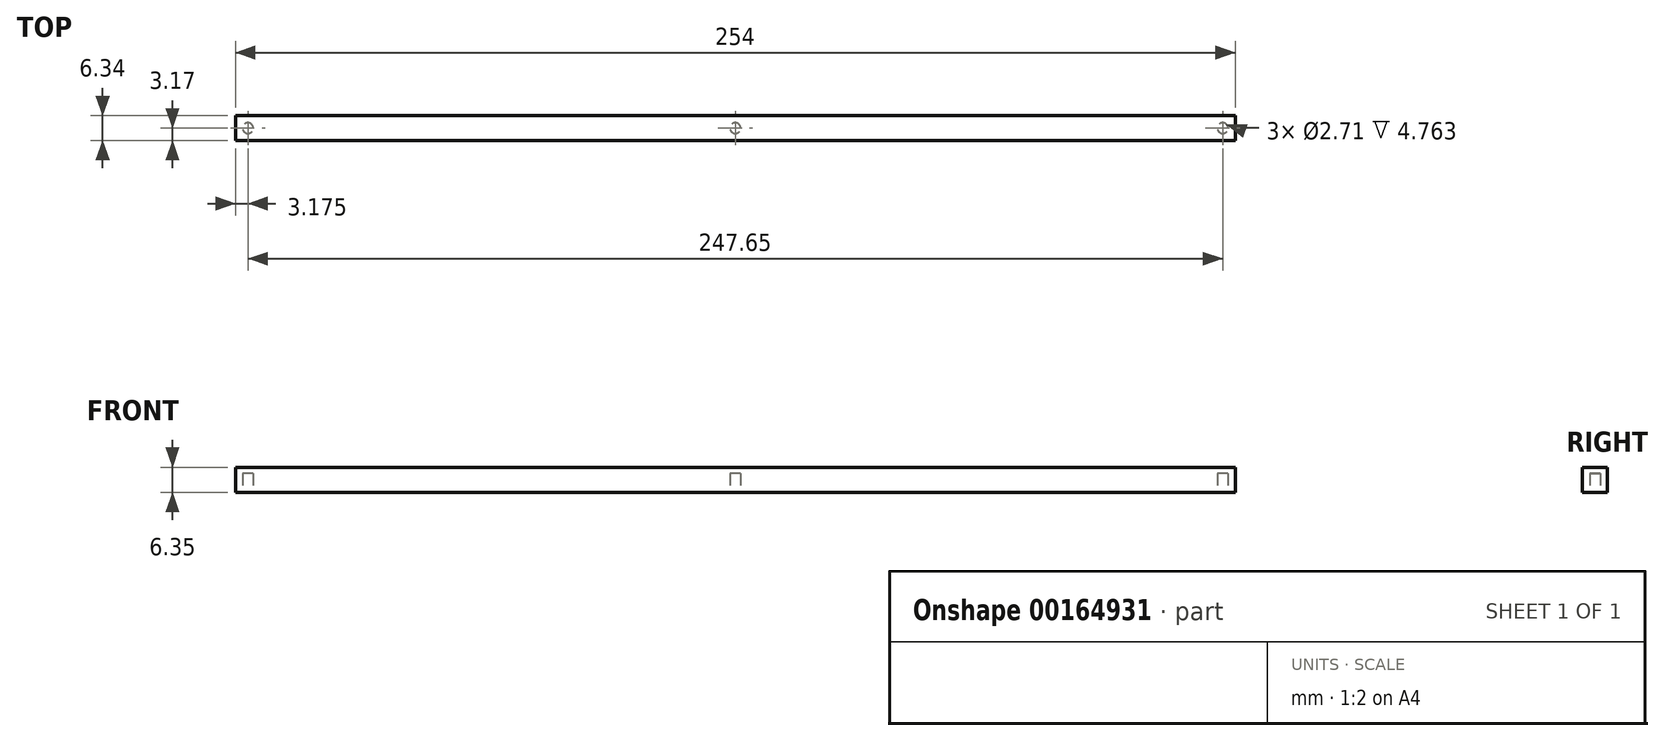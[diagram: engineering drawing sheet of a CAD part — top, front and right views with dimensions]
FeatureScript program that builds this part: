
annotation { "Feature Type Name" : "Feature", "Feature Type Description" : "" }
export const myFeature = defineFeature(function(context is Context, id is Id, definition is map)
    precondition{}
    {
        {
            var Q0;
            Q0=qCreatedBy(makeId("Top.planeOp"),FACE);
            var sketch = newSketch(context, id + "F0", { "sketchPlane" : qUnion([Q0])});
            skLineSegment(sketch, "E0.bottom", {"start": v(127, -3.17) * mm, "end": v(-127, -3.18) * mm});
            skLineSegment(sketch, "E0.top", {"start": v(127, 3.18) * mm, "end": v(-127, 3.17) * mm});
            skLineSegment(sketch, "E0.left", {"start": v(127, -3.17) * mm, "end": v(127, 3.18) * mm});
            skLineSegment(sketch, "E0.right", {"start": v(-127, -3.18) * mm, "end": v(-127, 3.17) * mm});
            skPoint(sketch, "E0.middle", {"position": v(0, 0) * mm});
            skCircle(sketch, "E1", {"center": v(0, 0) * mm, "radius": 1.35 * mm});
            skLineSegment(sketch, "E2", {"start": v(-127, 0) * mm, "end": v(-123.83, 0) * mm, "construction": true});
            skPoint(sketch, "E2.endSnap0", {"position": v(-127, 0) * mm});
            skLineSegment(sketch, "E3", {"start": v(-123.83, 0) * mm, "end": v(-123.83, 3.17) * mm, "construction": true});
            skLineSegment(sketch, "E4", {"start": v(127, 0) * mm, "end": v(123.82, 0) * mm, "construction": true});
            skPoint(sketch, "E4.endSnap0", {"position": v(127, 0) * mm});
            skCircle(sketch, "E5", {"center": v(-123.83, 0) * mm, "radius": 1.35 * mm});
            skCircle(sketch, "E6", {"center": v(123.82, 0) * mm, "radius": 1.35 * mm});
            skSolve(sketch);
        }
        {
            var Q0;
            Q0 = qSketchRegion(id + "F0", true);
            extrude(context, id + "F1", {"entities" : qUnion([Q0]), "depth" : 4.76 * mm});
        }
        {
            var Q0;
            Q0=makeQuery(id+"F1.opExtrude","CAP_FACE",FACE,{"disambiguationData":[OSD([sQuery(id+"F0.wireOp",EDGE,"E0.bottom"),sQuery(id+"F0.wireOp",EDGE,"E0.top"),sQuery(id+"F0.wireOp",EDGE,"E0.left"),sQuery(id+"F0.wireOp",EDGE,"E0.right"),sQuery(id+"F0.wireOp",EDGE,"E1"),sQuery(id+"F0.wireOp",EDGE,"E5"),sQuery(id+"F0.wireOp",EDGE,"E6")])],"isStart":false});
            var sketch = newSketch(context, id + "F2", { "sketchPlane" : qUnion([Q0])});
            skLineSegment(sketch, "E7.bottom", {"start": v(127, 3.18) * mm, "end": v(-127, 3.18) * mm});
            skLineSegment(sketch, "E7.top", {"start": v(127, -3.18) * mm, "end": v(-127, -3.18) * mm});
            skLineSegment(sketch, "E7.left", {"start": v(127, 3.18) * mm, "end": v(127, -3.18) * mm});
            skLineSegment(sketch, "E7.right", {"start": v(-127, 3.18) * mm, "end": v(-127, -3.18) * mm});
            skSolve(sketch);
        }
        {
            var Q0;
            Q0 = qSketchRegion(id + "F2", true);
            extrude(context, id + "F3", {"entities" : qUnion([Q0]), "operationType" : NewBodyOperationType.ADD, "depth" : 1.59 * mm});
        }
    });
